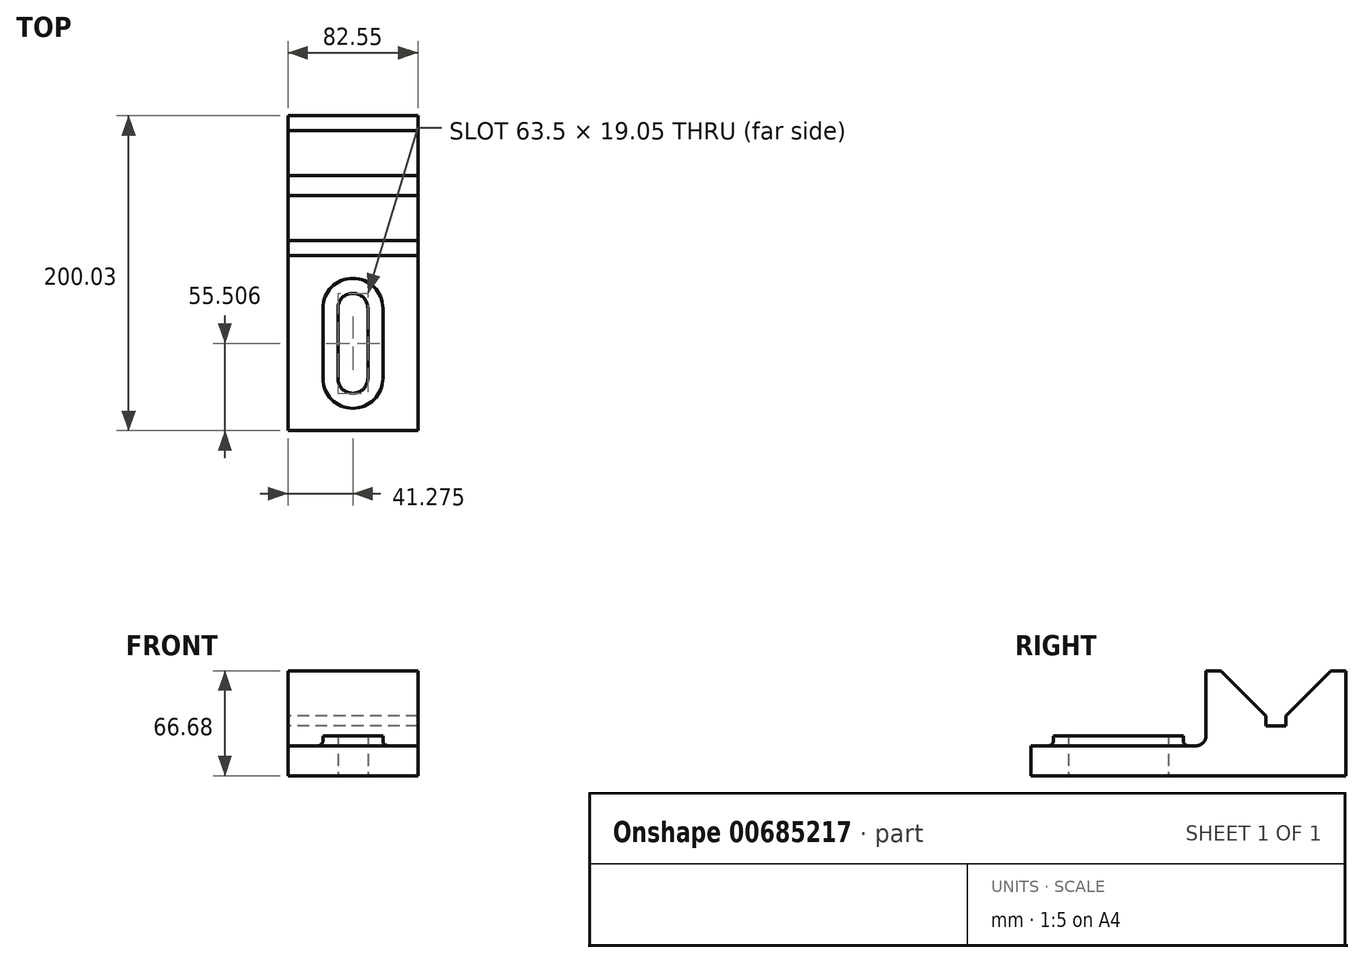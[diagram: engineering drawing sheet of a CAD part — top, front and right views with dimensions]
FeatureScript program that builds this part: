
annotation { "Feature Type Name" : "Feature", "Feature Type Description" : "" }
export const myFeature = defineFeature(function(context is Context, id is Id, definition is map)
    precondition{}
    {
        {
            var Q0;
            Q0=qCreatedBy(makeId("Front.planeOp"),FACE);
            var sketch = newSketch(context, id + "F0", { "sketchPlane" : qUnion([Q0])});
            skLineSegment(sketch, "E0.bottom", {"start": v(0, 0) * mm, "end": v(82.55, 0) * mm});
            skLineSegment(sketch, "E0.top", {"start": v(0, 66.68) * mm, "end": v(82.55, 66.68) * mm});
            skLineSegment(sketch, "E0.left", {"start": v(0, 0) * mm, "end": v(0, 66.68) * mm});
            skLineSegment(sketch, "E0.right", {"start": v(82.55, 0) * mm, "end": v(82.55, 66.68) * mm});
            skSolve(sketch);
        }
        {
            var Q0;
            Q0=makeQuery(id+"F0.imprint","IMPRINT",FACE,{"disambiguationData":[TD([[makeQuery(id+"F0.imprint","IMPRINT",EDGE,{"derivedFrom":sQuery(id+"F0.wireOp",EDGE,"E0.bottom")}),1.0]])]});
            extrude(context, id + "F1", {"entities" : qUnion([Q0]), "depth" : 200.02 * mm, "offsetDistance" : 25.4 * mm});
        }
        {
            var Q0;
            Q0=makeQuery(id+"F1.opExtrude","SWEPT_FACE",FACE,{"disambiguationData":[OSD([sQuery(id+"F0.wireOp",EDGE,"E0.left")])]});
            var sketch = newSketch(context, id + "F2", { "sketchPlane" : qUnion([Q0])});
            skLineSegment(sketch, "E1", {"start": v(200.03, 19.05) * mm, "end": v(88.9, 19.05) * mm});
            skLineSegment(sketch, "E2", {"start": v(88.9, 19.05) * mm, "end": v(88.9, 66.68) * mm});
            skLineSegment(sketch, "E3", {"start": v(88.9, 66.68) * mm, "end": v(200.03, 66.68) * mm});
            skLineSegment(sketch, "E4", {"start": v(200.03, 66.68) * mm, "end": v(200.03, 19.05) * mm});
            skSolve(sketch);
        }
        {
            var Q0;
            Q0=makeQuery(id+"F2.imprint","IMPRINT",FACE,{"disambiguationData":[TD([[makeQuery(id+"F2.imprint","IMPRINT",EDGE,{"derivedFrom":sQuery(id+"F2.wireOp",EDGE,"E1")}),-1.0]])]});
            extrude(context, id + "F3", {"entities" : qUnion([Q0]), "operationType" : NewBodyOperationType.REMOVE, "oppositeDirection" : true, "depth" : 101.6 * mm, "offsetDistance" : 25.4 * mm});
        }
        {
            var Q0;
            Q0=makeQuery(id+"F3.boolean.opBoolean","COPY",EDGE,{"derivedFrom":makeQuery(id+"F3.opExtrude","SWEPT_EDGE",EDGE,{"disambiguationData":[OSD([sQuery(id+"F2.wireOp",EDGE,"E1"),sQuery(id+"F2.wireOp",EDGE,"E2")])]})});
            fillet(context, id + "F4", {"entities" : qUnion([Q0]), "radius" : 6.35 * mm, "tangentPropagation" : true, "allowEdgeOverflow" : false});
        }
        {
            var Q0;
            Q0=makeQuery(id+"F3.boolean.opBoolean","COPY",FACE,{"derivedFrom":makeQuery(id+"F3.opExtrude","SWEPT_FACE",FACE,{"disambiguationData":[OSD([sQuery(id+"F2.wireOp",EDGE,"E1")])]})});
            var sketch = newSketch(context, id + "F5", { "sketchPlane" : qUnion([Q0])});
            skCircle(sketch, "E5", {"center": v(41.28, -122.3) * mm, "radius": 19.05 * mm});
            skCircle(sketch, "E6", {"center": v(41.28, -166.75) * mm, "radius": 19.05 * mm});
            skLineSegment(sketch, "E7", {"start": v(22.23, -166.75) * mm, "end": v(22.23, -122.3) * mm});
            skLineSegment(sketch, "E8", {"start": v(60.33, -122.3) * mm, "end": v(60.33, -166.75) * mm});
            skCircle(sketch, "E9", {"center": v(41.28, -122.3) * mm, "radius": 9.53 * mm});
            skCircle(sketch, "E10", {"center": v(41.28, -166.75) * mm, "radius": 9.53 * mm});
            skLineSegment(sketch, "E11", {"start": v(31.75, -122.3) * mm, "end": v(31.75, -166.75) * mm});
            skLineSegment(sketch, "E12", {"start": v(50.8, -166.75) * mm, "end": v(50.8, -122.3) * mm});
            skSolve(sketch);
        }
        {
            var Q0;
            {var subQ0=sQuery(id+"F5.wireOp",EDGE,"E5");var subQ1=makeQuery(id+"F5.imprint","INTERSECT",VERTEX,{"derivedFrom":[subQ0,sQuery(id+"F5.wireOp",EDGE,"E7")]});Q0=makeQuery(id+"F5.imprint","IMPRINT",FACE,{"disambiguationData":[TD([[makeQuery(id+"F5.imprint","IMPRINT",EDGE,{"disambiguationData":[TD([[subQ1,1.0]])],"derivedFrom":subQ0}),1.0]])]});}
            var Q1;
            {var subQ0=sQuery(id+"F5.wireOp",EDGE,"E7");Q1=makeQuery(id+"F5.imprint","IMPRINT",FACE,{"disambiguationData":[TD([[makeQuery(id+"F5.imprint","IMPRINT",EDGE,{"derivedFrom":subQ0}),-1.0]])]});}
            var Q2;
            {var subQ0=sQuery(id+"F5.wireOp",EDGE,"E8");Q2=makeQuery(id+"F5.imprint","IMPRINT",FACE,{"disambiguationData":[TD([[makeQuery(id+"F5.imprint","IMPRINT",EDGE,{"derivedFrom":subQ0}),-1.0]])]});}
            var Q3;
            {var subQ0=sQuery(id+"F5.wireOp",EDGE,"E6");var subQ1=makeQuery(id+"F5.imprint","INTERSECT",VERTEX,{"derivedFrom":[subQ0,sQuery(id+"F5.wireOp",EDGE,"E8")]});Q3=makeQuery(id+"F5.imprint","IMPRINT",FACE,{"disambiguationData":[TD([[makeQuery(id+"F5.imprint","IMPRINT",EDGE,{"disambiguationData":[TD([[subQ1,-1.0]])],"derivedFrom":subQ0}),1.0]])]});}
            extrude(context, id + "F6", {"entities" : qUnion([Q0, Q1, Q2, Q3]), "operationType" : NewBodyOperationType.ADD, "depth" : 6.35 * mm, "offsetDistance" : 25.4 * mm});
        }
        {
            var Q0;
            Q0=makeQuery(id+"F6.opExtrude","CAP_EDGE",EDGE,{"disambiguationData":[OSD([sQuery(id+"F5.wireOp",EDGE,"E7")])],"isStart":true});
            fillet(context, id + "F7", {"entities" : qUnion([Q0]), "radius" : 3.17 * mm, "tangentPropagation" : true, "allowEdgeOverflow" : false});
        }
        {
            var Q0;
            {var subQ0=sQuery(id+"F5.wireOp",EDGE,"E9");var subQ1=makeQuery(id+"F5.imprint","INTERSECT",VERTEX,{"derivedFrom":[subQ0,sQuery(id+"F5.wireOp",EDGE,"E11")]});Q0=makeQuery(id+"F5.imprint","IMPRINT",FACE,{"disambiguationData":[TD([[makeQuery(id+"F5.imprint","IMPRINT",EDGE,{"disambiguationData":[TD([[subQ1,1.0]])],"derivedFrom":subQ0}),1.0]])]});}
            var Q1;
            {var subQ0=sQuery(id+"F5.wireOp",EDGE,"E11");var subQ1=sQuery(id+"F5.wireOp",EDGE,"E5");var subQ2=makeQuery(id+"F5.imprint","INTERSECT",VERTEX,{"derivedFrom":[subQ1,subQ0]});Q1=makeQuery(id+"F5.imprint","IMPRINT",FACE,{"disambiguationData":[TD([[makeQuery(id+"F5.imprint","IMPRINT",EDGE,{"disambiguationData":[TD([[subQ2,-1.0]])],"derivedFrom":subQ1}),1.0]])]});}
            var Q2;
            {var subQ0=sQuery(id+"F5.wireOp",EDGE,"E11");var subQ1=sQuery(id+"F5.wireOp",EDGE,"E5");var subQ2=makeQuery(id+"F5.imprint","INTERSECT",VERTEX,{"derivedFrom":[subQ1,subQ0]});Q2=makeQuery(id+"F5.imprint","IMPRINT",FACE,{"disambiguationData":[TD([[makeQuery(id+"F5.imprint","IMPRINT",EDGE,{"disambiguationData":[TD([[subQ2,-1.0]])],"derivedFrom":subQ1}),-1.0]])]});}
            var Q3;
            {var subQ0=sQuery(id+"F5.wireOp",EDGE,"E12");var subQ1=sQuery(id+"F5.wireOp",EDGE,"E6");var subQ2=makeQuery(id+"F5.imprint","INTERSECT",VERTEX,{"derivedFrom":[subQ1,subQ0]});Q3=makeQuery(id+"F5.imprint","IMPRINT",FACE,{"disambiguationData":[TD([[makeQuery(id+"F5.imprint","IMPRINT",EDGE,{"disambiguationData":[TD([[subQ2,-1.0]])],"derivedFrom":subQ1}),1.0]])]});}
            var Q4;
            {var subQ0=sQuery(id+"F5.wireOp",EDGE,"E10");var subQ1=makeQuery(id+"F5.imprint","INTERSECT",VERTEX,{"derivedFrom":[subQ0,sQuery(id+"F5.wireOp",EDGE,"E11")]});Q4=makeQuery(id+"F5.imprint","IMPRINT",FACE,{"disambiguationData":[TD([[makeQuery(id+"F5.imprint","IMPRINT",EDGE,{"disambiguationData":[TD([[subQ1,1.0]])],"derivedFrom":subQ0}),1.0]])]});}
            extrude(context, id + "F8", {"entities" : qUnion([Q0, Q1, Q2, Q3, Q4]), "operationType" : NewBodyOperationType.REMOVE, "oppositeDirection" : true, "depth" : 25.4 * mm, "offsetDistance" : 25.4 * mm});
        }
        {
            var Q0;
            Q0=makeQuery(id+"F1.opExtrude","SWEPT_FACE",FACE,{"disambiguationData":[OSD([sQuery(id+"F0.wireOp",EDGE,"E0.left")])]});
            var sketch = newSketch(context, id + "F9", { "sketchPlane" : qUnion([Q0])});
            skLineSegment(sketch, "E13", {"start": v(0, 66.68) * mm, "end": v(9.53, 66.68) * mm});
            skLineSegment(sketch, "E14", {"start": v(9.53, 66.68) * mm, "end": v(44.45, 66.68) * mm});
            skLineSegment(sketch, "E15", {"start": v(9.52, 66.68) * mm, "end": v(44.45, 31.75) * mm});
            skLineSegment(sketch, "E16", {"start": v(44.45, 31.75) * mm, "end": v(44.45, 66.68) * mm});
            skLineSegment(sketch, "E17.MirrorCS", {"start": v(79.37, 66.68) * mm, "end": v(44.45, 31.75) * mm});
            skLineSegment(sketch, "E18.MirrorCS", {"start": v(79.37, 66.68) * mm, "end": v(44.45, 66.68) * mm});
            skLineSegment(sketch, "E19", {"start": v(79.37, 66.68) * mm, "end": v(88.9, 66.68) * mm});
            skLineSegment(sketch, "E20", {"start": v(44.45, 31.75) * mm, "end": v(38.1, 31.75) * mm});
            skLineSegment(sketch, "E21", {"start": v(44.45, 31.75) * mm, "end": v(50.8, 31.75) * mm});
            skLineSegment(sketch, "E22", {"start": v(50.8, 31.75) * mm, "end": v(50.8, 38.1) * mm});
            skLineSegment(sketch, "E23", {"start": v(38.1, 31.75) * mm, "end": v(38.1, 38.1) * mm});
            skLineSegment(sketch, "E24", {"start": v(38.1, 38.1) * mm, "end": v(50.8, 38.1) * mm});
            skSolve(sketch);
        }
        {
            var Q0;
            {var subQ0=sQuery(id+"F9.wireOp",EDGE,"E16");var subQ3=sQuery(id+"F9.wireOp",EDGE,"E24");var subQ5=makeQuery(id+"F9.imprint","INTERSECT",VERTEX,{"derivedFrom":[subQ0,subQ3]});Q0=makeQuery(id+"F9.imprint","IMPRINT",FACE,{"disambiguationData":[TD([[makeQuery(id+"F9.imprint","IMPRINT",EDGE,{"disambiguationData":[TD([[subQ5,1.0]])],"derivedFrom":subQ3}),-1.0]])]});}
            var Q1;
            {var subQ0=sQuery(id+"F9.wireOp",EDGE,"E20");Q1=makeQuery(id+"F9.imprint","IMPRINT",FACE,{"disambiguationData":[TD([[makeQuery(id+"F9.imprint","IMPRINT",EDGE,{"derivedFrom":subQ0}),-1.0]])]});}
            var Q2;
            {var subQ1=sQuery(id+"F9.wireOp",EDGE,"E16");var subQ3=sQuery(id+"F9.wireOp",EDGE,"E24");var subQ4=makeQuery(id+"F9.imprint","INTERSECT",VERTEX,{"derivedFrom":[subQ1,subQ3]});Q2=makeQuery(id+"F9.imprint","IMPRINT",FACE,{"disambiguationData":[TD([[makeQuery(id+"F9.imprint","IMPRINT",EDGE,{"disambiguationData":[TD([[subQ4,-1.0]])],"derivedFrom":subQ3}),-1.0]])]});}
            var Q3;
            {var subQ0=sQuery(id+"F9.wireOp",EDGE,"E21");Q3=makeQuery(id+"F9.imprint","IMPRINT",FACE,{"disambiguationData":[TD([[makeQuery(id+"F9.imprint","IMPRINT",EDGE,{"derivedFrom":subQ0}),1.0]])]});}
            extrude(context, id + "F10", {"entities" : qUnion([Q0, Q1, Q2, Q3]), "operationType" : NewBodyOperationType.REMOVE, "oppositeDirection" : true, "depth" : 101.6 * mm, "offsetDistance" : 25.4 * mm});
        }
        {
            var Q0;
            {var subQ0=sQuery(id+"F9.wireOp",EDGE,"E14");Q0=makeQuery(id+"F9.imprint","IMPRINT",FACE,{"disambiguationData":[TD([[makeQuery(id+"F9.imprint","IMPRINT",EDGE,{"derivedFrom":subQ0}),1.0]])]});}
            var Q1;
            {var subQ0=sQuery(id+"F9.wireOp",EDGE,"E18.MirrorCS");Q1=makeQuery(id+"F9.imprint","IMPRINT",FACE,{"disambiguationData":[TD([[makeQuery(id+"F9.imprint","IMPRINT",EDGE,{"derivedFrom":subQ0}),1.0]])]});}
            extrude(context, id + "F11", {"entities" : qUnion([Q0, Q1]), "operationType" : NewBodyOperationType.REMOVE, "oppositeDirection" : true, "depth" : 101.6 * mm, "offsetDistance" : 25.4 * mm});
        }
    });
